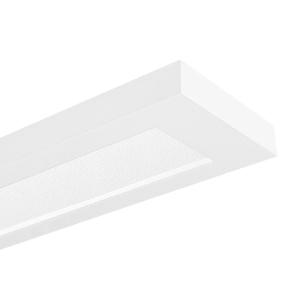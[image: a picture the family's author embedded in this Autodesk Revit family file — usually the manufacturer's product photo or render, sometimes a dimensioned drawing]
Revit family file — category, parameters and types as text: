
# Revit family: 3f_filippi_-_3f_travetta_di_lgs_3f_filippi_-_11630_-_3f_travetta_led_di_2x30w_dali_lgs_l1590
name_source: partatom
category: Lighting Fixtures
units: mm (PartAtom-declared; Revit-internal decimal feet)

## family parameters
Cut with Voids When Loaded = No
Host = Face
Light Source = No
Part Type = Normal
Room Calculation Point = No
Round Connector Dimension = Use Diameter
Shared = No

## types (1)
- 3F Filippi - 3F Travetta DI LGS (1 x LED, 6403 lm, 66 W, 4000 K)
    Apparent Load = 66 VA
    Approval mark = ENEC
    CIE Flux Codes = 64 93 99 85 100
    Color Rendering = 80
    Color Temperature = 4000 K
    Control Gear = Electronic transformer
    Default Elevation = 1800 mm
    Description = ILLUMINOTECHNICAL
Luminous efficiency 100% (DLOR 85%, ULOR 15%).
Initial luminous flux of the luminaire 6403 lm.
Symmetric direct-indirect distribution.
Installation Interdistance Transv.D = 1.18 x hu - Long.D = 1.18 x hu.
Average luminance <3000 cd/m² for radial angles >65°.
Tabular UGR (CIE 117 - 4H-8H; S=0.25H; 70/50/20): RUG 18 - 18.6.
Beam angle: 89° - 91°.
Luminous efficacy 97 lm/W.
Lifetime (L93/B10): 30000 h. (tq+25°C)
Lifetime (L90/B10): 50000 h. (tq+25°C)
Lifetime (L85/B10): 80000 h. (tq+25°C)
Lifetime (L80/B10): 100000 h. (tq+25°C)
Sudden decreased luminous flux after 50000 hours: 0% (C0).
Photobiological safety in compliance with IEC/TR 62778: RG0 risk exempt, (IEC 62471).
In compliance with IEC/EN 62722-2-1 - IEC/EN 62717 standards.

SOURCE
2 linear LED modules 30W/840.
Energy efficiency class (UE 2019/2020 - UE 2019/2015): D.
CIE 13.3 Colour rendering index: CRI >80 (R9 <50%).
IES TM-30 Fidelity Index: Rf = 84 Rg = 95.
CCT nominal colour temperature 4000 K.
Colour initial tolerance (MacAdam): SDCM 2.

MECHANICAL
Housing with squared shape in white painted galvannealed steel, with nonreflecting surface.
Flow recuperator in semi-glossy aluminium.
LGS micro-prismatic flat diffuser in transparent methacrylate (PMMA), multi-lenticular exterior, anti-glare.
Anti-glare opal polycarbonate filter for brightness uniformity.
Upper holes closing film made of opal polycarbonate.
Luminaire with limited surface temperature. - D - (EN 60598-2-24)
Dimensions: 1590x190 mm, height 60 mm. Weight 5.6 kg.
IP20 protection degree.
Glow-wire test resistance 650°C.

ELECTRICAL
Halogen Free DALI-2 DATI (Parts 251, 252, 253), PUSH-DIM, electronic wiring 230V-50/60Hz, power factor 0.95 at full load, THD <25%, constant output current, SELV, class I, 1 driver, 1 DALI addresse.
Power of the luminaire 66 W.
CE - IEC 60598-1 - EN 60598-1.
SAFE FLICKER: PstLM=<1 and SVM=<0.4 (IEC TR 61547-1 and IEC TR 63158), to ensure a more comfortable and safe light.
Luminaire compliant with EN 60598-2-22 for power supply from a centralised emergency system CPSS (Central Power Supply System), not incorporated in the luminaire - high risk areas excluded. The default power and flux are 100% in AC and 15% in DC.
Ambient temperature from 0°C to +25°C.
Temperature class T6 max 85°C.
Relative humidity UR: <85%.

INSTALLATION
Suspended.
All accessories dedicated to this product are available on the Catalog and on our website www.3F-Filippi.com.

APPLICATIONS
In environments, even with reduced height, requiring a comfortable light.
In environments with VDTs, managerial offices and staterooms, public offices and schools.

LIGHT MANAGEMENT
Recommended minimum setting: 10%.
The luminaire, equipped with (DALI-2 DATI) driver, can be controlled manually with 3F Easy Dim technology or automatically/manually with wired or wireless DALI/D2D control systems.
The D2D driver guarantees interoperability with other devices with the same certification by making the following information available:
Device Data (Part 251), Energy Report (Part 252), Diagnosis & Maintenance (Part 253).
In electrical systems without a regulation system (manual or automatic) and DALI bus, a suitable jumper must be made on the DA-DA terminals of the appliance.

WARNING
Luminaire designed for disposal/recycling at end-of-life.
Replaceable (LED only) light source by a professional. Replaceable control gear by a professional.
    Height = 60 mm  [stored 0.19685 ft]
    Lamp = 1 x LED
    Lamp Light Flux = 6403 lm
    Lamp Power = 66 W
    Lamp count = 1
    Length = 1590 mm
    Lifetime = 50000 h
    Luminous efficacy = 97 lm/W
    Manufacturer = 3F Filippi
    ModVariant = No
    Model = 3F Filippi - 11630 - 3F Travetta LED DI 2x30W DALI LGS L1590
    Mounting Place = Ceiling
    Mounting Type = Pendant
    Number of Poles = 1
    OnlyDefault = Yes
    Power Factor = 1
    Product Name = 3F Filippi - 3F Travetta DI LGS
    Product group = pendant luminaire
    ProductGroupID = 9
    Protection Class = Protection class I
    Protection Degree = IP 20
    RLX_Detail_Level = 1
    RLX_Emergency_Light_Flux = 0 lm
    RLX_Emergency_Type = 0
    RLX_Emergency_Type_DB = No
    RlxData = <blob elided: 52653 chars, md5=0b56f3c9>
    Socket = socket
    Standby Power = 0 W
    System Light Flux = 6403 lm
    System Power = 66 W
    Type Comments = Product without accessories
    Type Image = 3ffilippi_3f_travetta_led_lgs.jpg
    URL = http://relux.com
    VarID = ---
    Voltage = 0 V
    Weight = 0.00 kg
    Width = 190 mm  [stored 0.62336 ft]

note: [stored X ft] marks values corroborated as IEEE doubles in the binary element streams (Revit-internal decimal feet)

## geometry (parser evidence)
native form markers: Blend x4, Sweep x13
no freeform markers — native parametric forms only
